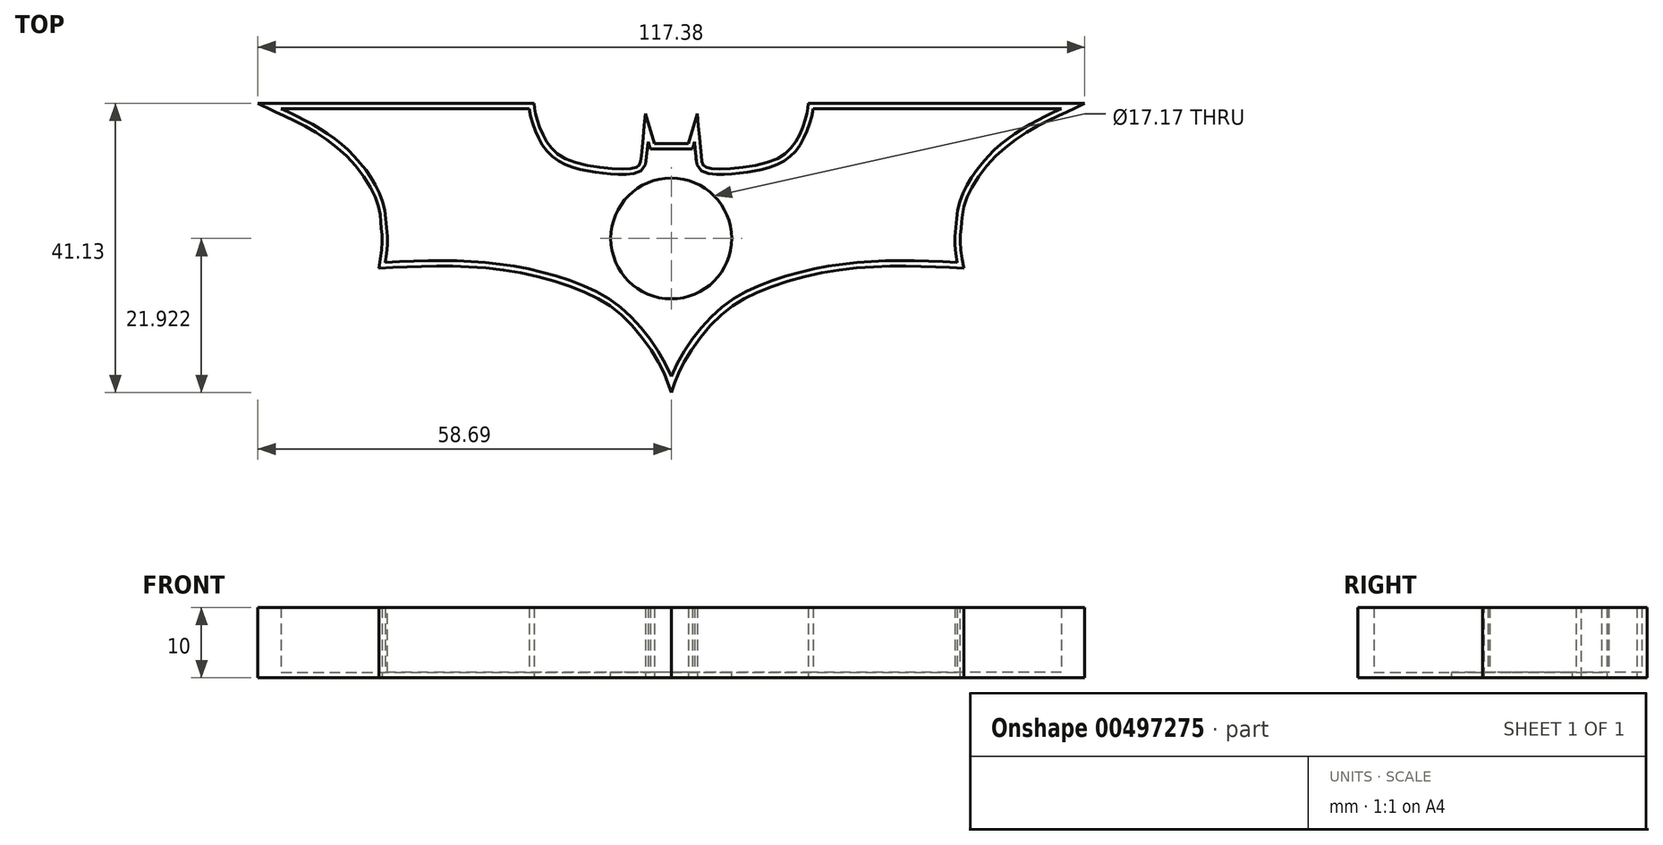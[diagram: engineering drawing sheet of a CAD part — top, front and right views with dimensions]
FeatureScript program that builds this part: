
annotation { "Feature Type Name" : "Feature", "Feature Type Description" : "" }
export const myFeature = defineFeature(function(context is Context, id is Id, definition is map)
    precondition{}
    {
        {
            var Q0;
            Q0=qCreatedBy(makeId("Top.planeOp"),FACE);
            var sketch = newSketch(context, id + "F0", { "sketchPlane" : qUnion([Q0])});
            skLineSegment(sketch, "E0", {"start": v(-58.7, 17.25) * mm, "end": v(-19.48, 17.25) * mm});
            skLineSegment(sketch, "E1", {"start": v(-3.68, 15.76) * mm, "end": v(-2.41, 11.51) * mm});
            skLineSegment(sketch, "E2", {"start": v(-2.41, 11.51) * mm, "end": v(0, 11.51) * mm});
            skFitSpline(sketch, "E3", {"points": [v(-19.48, 17.25) * mm, v(-19.2, 15.49) * mm, v(-17.86, 12.1) * mm, v(-14.61, 9.2) * mm, v(-6.45, 7.92) * mm, v(-4.59, 8.4) * mm, v(-4.3, 9.45) * mm, v(-3.68, 15.76) * mm], "startDerivative": vector(1.7, -15.86) * mm, "endDerivative": vector(3.77, 39.6) * mm});
            skFitSpline(sketch, "E4", {"points": [v(-58.7, 17.25) * mm, v(-57.25, 16.5) * mm, v(-52.44, 14.22) * mm, v(-45.62, 9.27) * mm, v(-41.67, 2.97) * mm, v(-41.23, 0) * mm, v(-41.04, -2.29) * mm, v(-41.52, -6.16) * mm], "startDerivative": vector(13.9, -7.82) * mm, "endDerivative": vector(-5.2, -30.31) * mm});
            skFitSpline(sketch, "E5", {"points": [v(0, -23.88) * mm, v(-1.65, -19.85) * mm, v(-6.7, -13.2) * mm, v(-13.17, -9.2) * mm, v(-23.67, -6.46) * mm, v(-33.87, -5.88) * mm, v(-41.52, -6.16) * mm], "startDerivative": vector(-10.1, 30.63) * mm, "endDerivative": vector(-45.44, -2.3) * mm});
            skLineSegment(sketch, "E6.MirrorCS", {"start": v(2.41, 11.51) * mm, "end": v(0, 11.51) * mm});
            skLineSegment(sketch, "E7.MirrorCS", {"start": v(3.68, 15.76) * mm, "end": v(2.41, 11.51) * mm});
            skFitSpline(sketch, "E8.MirrorCS", {"points": [v(19.48, 17.25) * mm, v(19.2, 15.49) * mm, v(17.86, 12.1) * mm, v(14.61, 9.2) * mm, v(6.45, 7.92) * mm, v(4.59, 8.4) * mm, v(4.3, 9.45) * mm, v(3.68, 15.76) * mm], "startDerivative": vector(-1.7, -15.86) * mm, "endDerivative": vector(-3.77, 39.6) * mm});
            skFitSpline(sketch, "E9.MirrorCS", {"points": [v(58.7, 17.25) * mm, v(57.25, 16.5) * mm, v(52.44, 14.22) * mm, v(45.62, 9.27) * mm, v(41.67, 2.97) * mm, v(41.23, 0) * mm, v(41.04, -2.29) * mm, v(41.52, -6.16) * mm], "startDerivative": vector(-13.9, -7.82) * mm, "endDerivative": vector(5.2, -30.31) * mm});
            skLineSegment(sketch, "E10.MirrorCS", {"start": v(58.7, 17.25) * mm, "end": v(19.48, 17.25) * mm});
            skFitSpline(sketch, "E11.MirrorCS", {"points": [v(0, -23.88) * mm, v(1.65, -19.85) * mm, v(6.7, -13.2) * mm, v(13.17, -9.2) * mm, v(23.67, -6.46) * mm, v(33.87, -5.88) * mm, v(41.52, -6.16) * mm], "startDerivative": vector(10.1, 30.63) * mm, "endDerivative": vector(45.44, -2.3) * mm});
            skSolve(sketch);
        }
        {
            var Q0;
            Q0=makeQuery(id+"F0.imprint","IMPRINT",FACE,{"disambiguationData":[TD([[makeQuery(id+"F0.imprint","IMPRINT",EDGE,{"derivedFrom":sQuery(id+"F0.wireOp",EDGE,"E0")}),-1.0]])]});
            extrude(context, id + "F1", {"entities" : qUnion([Q0]), "depth" : 10 * mm});
        }
        {
            var Q0;
            Q0=makeQuery(id+"F1.opExtrude","CAP_FACE",FACE,{"disambiguationData":[OSD([sQuery(id+"F0.wireOp",EDGE,"E0"),sQuery(id+"F0.wireOp",EDGE,"E1"),sQuery(id+"F0.wireOp",EDGE,"E2"),sQuery(id+"F0.wireOp",EDGE,"E3"),sQuery(id+"F0.wireOp",EDGE,"E4"),sQuery(id+"F0.wireOp",EDGE,"E5"),sQuery(id+"F0.wireOp",EDGE,"E6.MirrorCS"),sQuery(id+"F0.wireOp",EDGE,"E7.MirrorCS"),sQuery(id+"F0.wireOp",EDGE,"E8.MirrorCS"),sQuery(id+"F0.wireOp",EDGE,"E9.MirrorCS"),sQuery(id+"F0.wireOp",EDGE,"E10.MirrorCS"),sQuery(id+"F0.wireOp",EDGE,"E11.MirrorCS")])],"isStart":false});
            shell(context, id + "F2", {"entities" : qUnion([Q0]), "thickness" : 0.76 * mm});
        }
        {
            var Q0;
            Q0=makeQuery(id+"F2.opShell","OFFSET_FACE",FACE,{"disambiguationData":[OSD([sQuery(id+"F0.wireOp",EDGE,"E0"),sQuery(id+"F0.wireOp",EDGE,"E1"),sQuery(id+"F0.wireOp",EDGE,"E2"),sQuery(id+"F0.wireOp",EDGE,"E3"),sQuery(id+"F0.wireOp",EDGE,"E4"),sQuery(id+"F0.wireOp",EDGE,"E5"),sQuery(id+"F0.wireOp",EDGE,"E6.MirrorCS"),sQuery(id+"F0.wireOp",EDGE,"E7.MirrorCS"),sQuery(id+"F0.wireOp",EDGE,"E8.MirrorCS"),sQuery(id+"F0.wireOp",EDGE,"E9.MirrorCS"),sQuery(id+"F0.wireOp",EDGE,"E10.MirrorCS"),sQuery(id+"F0.wireOp",EDGE,"E11.MirrorCS")])]});
            var sketch = newSketch(context, id + "F3", { "sketchPlane" : qUnion([Q0])});
            skCircle(sketch, "E12", {"center": v(0, -1.96) * mm, "radius": 8.58 * mm});
            skSolve(sketch);
        }
        {
            var Q0;
            Q0=makeQuery(id+"F3.imprint","IMPRINT",FACE,{"disambiguationData":[TD([[makeQuery(id+"F3.imprint","IMPRINT",EDGE,{"derivedFrom":sQuery(id+"F3.wireOp",EDGE,"E12")}),1.0]])]});
            extrude(context, id + "F4", {"entities" : qUnion([Q0]), "operationType" : NewBodyOperationType.REMOVE, "oppositeDirection" : true, "depth" : 25.4 * mm});
        }
    });
